# Revit family: ORBH(QA)
name_source: partatom
category: Mechanical Equipment
units: mm (PartAtom-declared; Revit-internal decimal feet)

## family parameters
Always vertical = Yes
Cut with Voids When Loaded = No
OmniClass Number = 23.40.40.11.17
OmniClass Title = Refrigerated Cases
Part Type = Normal
Room Calculation Point = No
Round Connector Dimension = Use Radius
Shared = No
Work Plane-Based = Yes

## types (10) — shared parameters
27" Shelf = Yes
ANTI SWEAT APPARENT LOAD = 0 VA
Application Discipline = Beverage
BTUH Conventional = 549
BTUH Parallel = 519
Certifications = NSF 7, UL471, CSA
DATE = 12/21/2015
DISCHARGE AIR TEMP = 380 °F
DISCHARGE AIR VELOCITY = 34 °F
Default Elevation = 48"
Defrost Num Day = 4
Defrost Termination = 47 °F
Defrost Type = TIMED-OFF DEFROST
Defrosts Per Day_2 = 4
Description = HIGH REACH-IN GLASS DOOR MERCHANIDER
Discharge Air (°F) = 38° F
Discharge Air Velocity (FPM) = 215
EQUIPMENT DESCRIPTION = HIGH REACH-IN GLASS DOOR MERCHANIDER
EQUIPMENT MARK = ORBH
Evap Temp = 28
Evaporator (°F) = 34° F
GLASS = Glass
Height = 85"
Item Description = HIGH REACH-IN GLASS DOOR MERCHANIDER
Legend Number = ORBH
Load Mbh = 0.675
Manufacturer = HILL PHOENIX
Model = ORBH
NUMBER FOR GUIDLINES AND CONTROL ORGANIZATION = 1
PAINTED METAL UPPER SHELF = PAINTED SHELVES
Refrig Charge Lbs = 0
Size of Door = 30"
Superheat Set Point @ Bulb (°F) = 4 - 6
TIMED OFF DEFROST FAIL-SAFE (Min) = 30
TIMED OFF DEFROST TERMINATION TEMP = 47 °F
Timed-Off Defrost Fail-Safe (Min) = 30 (Min)
Timed-Off Defrost Termination Temp_2 = 47° F
URL = http://www.hillphoenix.com
Vista Optimax Pro Amps = 0 A
Vista Optimax Pro Watts = 0 W
Width = 42"
set 3 biswing doors = No

## per-type parameters (varying)
- 1-Door-30"-Beverage: 101 Amps=0 A; 101 Watts=22 W; CENTER LINE & DRAIN=15 1/2"; Crossfire/Polaris Amps=0 A; Crossfire/Polaris Watts=15 W; DOOR CONFIGURATION=MASTER DOOR.0002 : 30" X 68 3/8" 1 DOOR A SWING (LEFT OPENING); Eliminaator Amps=0 A; Eliminaator Watts=22 W; GE Immersion Amps=0 A; GE Immersion Watts=16 W; High Efficiency Amps=0 A; High Efficiency Watts=26 W; Length=31"; Length of Cases=31"; NUMBER FOR ELECTRICAL DATA=1; NUMBER FOR LIGHTING DATA=1; NUMBER OF DOORS=1; Number of Fans=1; Number of Fans per Case=1; Optimax Pro Amps=0 A; Optimax Pro Watts=10 W; Type of Door Swing=A-Swing; Vista-C/60 Amps=0 A; Vista-C/60 Watts=34 W; one door box=2 3/16"; right side single door=Yes; set 1 biswing doors=No; set 2 biswing doors=No
- 2-Door-30"-Beverage: 101 Amps=0 A; 101 Watts=43 W; CENTER LINE & DRAIN=30"; Crossfire/Polaris Amps=0 A; Crossfire/Polaris Watts=30 W; DOOR CONFIGURATION=MASTER DOOR.0002 : 30" X 68 3/8" 2 DOOR A SWING (LEFT OPENING); Eliminaator Amps=0 A; Eliminaator Watts=43 W; GE Immersion Amps=0 A; GE Immersion Watts=32 W; High Efficiency Amps=0 A; High Efficiency Watts=26 W; Length=60"; Length of Cases=60"; NUMBER FOR ELECTRICAL DATA=2; NUMBER FOR LIGHTING DATA=2; NUMBER OF DOORS=2; Number of Fans=1; Number of Fans per Case=1; Optimax Pro Amps=0 A; Optimax Pro Watts=20 W; Type of Door Swing=B-Swing; Vista-C/60 Amps=1 A; Vista-C/60 Watts=68 W; one door box=5"; right side single door=Yes; set 1 biswing doors=No; set 2 biswing doors=No
- 3-Door-30"-Beverage: 101 Amps=1 A; 101 Watts=66 W; CENTER LINE & DRAIN=45"; Crossfire/Polaris Amps=0 A; Crossfire/Polaris Watts=45 W; DOOR CONFIGURATION=MASTER DOOR.0002 : 30" X 68 3/8" 3 DOOR A SWING (LEFT OPENING); Eliminaator Amps=1 A; Eliminaator Watts=66 W; GE Immersion Amps=0 A; GE Immersion Watts=48 W; High Efficiency Amps=0 A; High Efficiency Watts=52 W; Length=90"; Length of Cases=90"; NUMBER FOR ELECTRICAL DATA=3; NUMBER FOR LIGHTING DATA=3; NUMBER OF DOORS=3; Number of Fans=2; Number of Fans per Case=2; Optimax Pro Amps=0 A; Optimax Pro Watts=31 W; Type of Door Swing=A-Swing; Vista-C/60 Amps=1 A; Vista-C/60 Watts=91 W; one door box=5"; right side single door=Yes; set 1 biswing doors=No; set 2 biswing doors=No
- 4-Door-30"-Beverage: 101 Amps=1 A; 101 Watts=90 W; CENTER LINE & DRAIN=60"; Crossfire/Polaris Amps=1 A; Crossfire/Polaris Watts=60 W; DOOR CONFIGURATION=MASTER DOOR.0002 : 30" X 68 3/8" 4 DOOR A SWING (LEFT OPENING); Eliminaator Amps=1 A; Eliminaator Watts=90 W; GE Immersion Amps=1 A; GE Immersion Watts=64 W; High Efficiency Amps=0 A; High Efficiency Watts=52 W; Length=120"; Length of Cases=120"; NUMBER FOR ELECTRICAL DATA=4; NUMBER FOR LIGHTING DATA=4; NUMBER OF DOORS=4; Number of Fans=2; Number of Fans per Case=2; Optimax Pro Amps=0 A; Optimax Pro Watts=41 W; Type of Door Swing=B-Swing; Vista-C/60 Amps=1 A; Vista-C/60 Watts=111 W; one door box=5"; right side single door=No; set 1 biswing doors=No; set 2 biswing doors=No
- 5-Door-30"-Beverage: 101 Amps=1 A; 101 Watts=113 W; CENTER LINE & DRAIN=75"; Crossfire/Polaris Amps=1 A; Crossfire/Polaris Watts=75 W; DOOR CONFIGURATION=MASTER DOOR.0002 : 30" X 68 3/8" 5 DOOR A SWING (LEFT OPENING); Eliminaator Amps=1 A; Eliminaator Watts=113 W; GE Immersion Amps=1 A; GE Immersion Watts=80 W; High Efficiency Amps=1 A; High Efficiency Watts=78 W; Length=150"; Length of Cases=150"; NUMBER FOR ELECTRICAL DATA=5; NUMBER FOR LIGHTING DATA=5; NUMBER OF DOORS=5; Number of Fans=3; Number of Fans per Case=3; Optimax Pro Amps=0 A; Optimax Pro Watts=51 W; Type of Door Swing=A-Swing; Vista-C/60 Amps=1 A; Vista-C/60 Watts=134 W; one door box=5"; right side single door=Yes; set 1 biswing doors=No; set 2 biswing doors=Yes
- 6-Door-30"-Beverage: 101 Amps=1 A; 101 Watts=138 W; CENTER LINE & DRAIN=90"; Crossfire/Polaris Amps=1 A; Crossfire/Polaris Watts=90 W; DOOR CONFIGURATION=MASTER DOOR.0002 : 30" X 68 3/8" 6 DOOR A SWING (LEFT OPENING); Eliminaator Amps=1 A; Eliminaator Watts=138 W; GE Immersion Amps=1 A; GE Immersion Watts=96 W; High Efficiency Amps=1 A; High Efficiency Watts=78 W; Length=180"; Length of Cases=180"; NUMBER FOR ELECTRICAL DATA=6; NUMBER FOR LIGHTING DATA=6; NUMBER OF DOORS=6; Number of Fans=3; Number of Fans per Case=3; Optimax Pro Amps=1 A; Optimax Pro Watts=61 W; Type of Door Swing=B-Swing; Vista-C/60 Amps=1 A; Vista-C/60 Watts=159 W; one door box=5"; right side single door=Yes; set 1 biswing doors=Yes; set 2 biswing doors=No
- 4': 101 Amps=1 A; 101 Watts=138 W; CENTER LINE & DRAIN=24"; Crossfire/Polaris Amps=1 A; Crossfire/Polaris Watts=90 W; DOOR CONFIGURATION=MASTER DOOR.0002 : 4'; Eliminaator Amps=1 A; Eliminaator Watts=138 W; GE Immersion Amps=1 A; GE Immersion Watts=96 W; High Efficiency Amps=1 A; High Efficiency Watts=78 W; Length=48"; Length of Cases=48"; NUMBER FOR ELECTRICAL DATA=6; NUMBER FOR LIGHTING DATA=6; NUMBER OF DOORS=6; Number of Fans=3; Number of Fans per Case=3; Optimax Pro Amps=1 A; Optimax Pro Watts=61 W; Type of Door Swing=B-Swing; Vista-C/60 Amps=1 A; Vista-C/60 Watts=159 W; one door box=5"; right side single door=Yes; set 1 biswing doors=Yes; set 2 biswing doors=No
- 6': 101 Amps=1 A; 101 Watts=138 W; CENTER LINE & DRAIN=36"; Crossfire/Polaris Amps=1 A; Crossfire/Polaris Watts=90 W; DOOR CONFIGURATION=MASTER DOOR.0002 : 6'; Eliminaator Amps=1 A; Eliminaator Watts=138 W; GE Immersion Amps=1 A; GE Immersion Watts=96 W; High Efficiency Amps=1 A; High Efficiency Watts=78 W; Length=72"; Length of Cases=72"; NUMBER FOR ELECTRICAL DATA=6; NUMBER FOR LIGHTING DATA=6; NUMBER OF DOORS=6; Number of Fans=3; Number of Fans per Case=3; Optimax Pro Amps=1 A; Optimax Pro Watts=61 W; Type of Door Swing=B-Swing; Vista-C/60 Amps=1 A; Vista-C/60 Watts=159 W; one door box=5"; right side single door=Yes; set 1 biswing doors=Yes; set 2 biswing doors=No
- 8': 101 Amps=1 A; 101 Watts=138 W; CENTER LINE & DRAIN=48"; Crossfire/Polaris Amps=1 A; Crossfire/Polaris Watts=90 W; DOOR CONFIGURATION=MASTER DOOR.0002 : 8'; Eliminaator Amps=1 A; Eliminaator Watts=138 W; GE Immersion Amps=1 A; GE Immersion Watts=96 W; High Efficiency Amps=1 A; High Efficiency Watts=78 W; Length=96"; Length of Cases=96"; NUMBER FOR ELECTRICAL DATA=6; NUMBER FOR LIGHTING DATA=6; NUMBER OF DOORS=6; Number of Fans=3; Number of Fans per Case=3; Optimax Pro Amps=1 A; Optimax Pro Watts=61 W; Type of Door Swing=B-Swing; Vista-C/60 Amps=1 A; Vista-C/60 Watts=159 W; one door box=5"; right side single door=Yes; set 1 biswing doors=Yes; set 2 biswing doors=No
- 12': 101 Amps=1 A; 101 Watts=138 W; CENTER LINE & DRAIN=72"; Crossfire/Polaris Amps=1 A; Crossfire/Polaris Watts=90 W; DOOR CONFIGURATION=MASTER DOOR.0002 : 12'; Eliminaator Amps=1 A; Eliminaator Watts=138 W; GE Immersion Amps=1 A; GE Immersion Watts=96 W; High Efficiency Amps=1 A; High Efficiency Watts=78 W; Length=144"; Length of Cases=144"; NUMBER FOR ELECTRICAL DATA=6; NUMBER FOR LIGHTING DATA=6; NUMBER OF DOORS=6; Number of Fans=3; Number of Fans per Case=3; Optimax Pro Amps=1 A; Optimax Pro Watts=61 W; Type of Door Swing=B-Swing; Vista-C/60 Amps=1 A; Vista-C/60 Watts=159 W; one door box=5"; right side single door=Yes; set 1 biswing doors=Yes; set 2 biswing doors=No

## geometry (parser evidence)
native form markers: Blend x10, Sweep x20
no freeform markers — native parametric forms only
